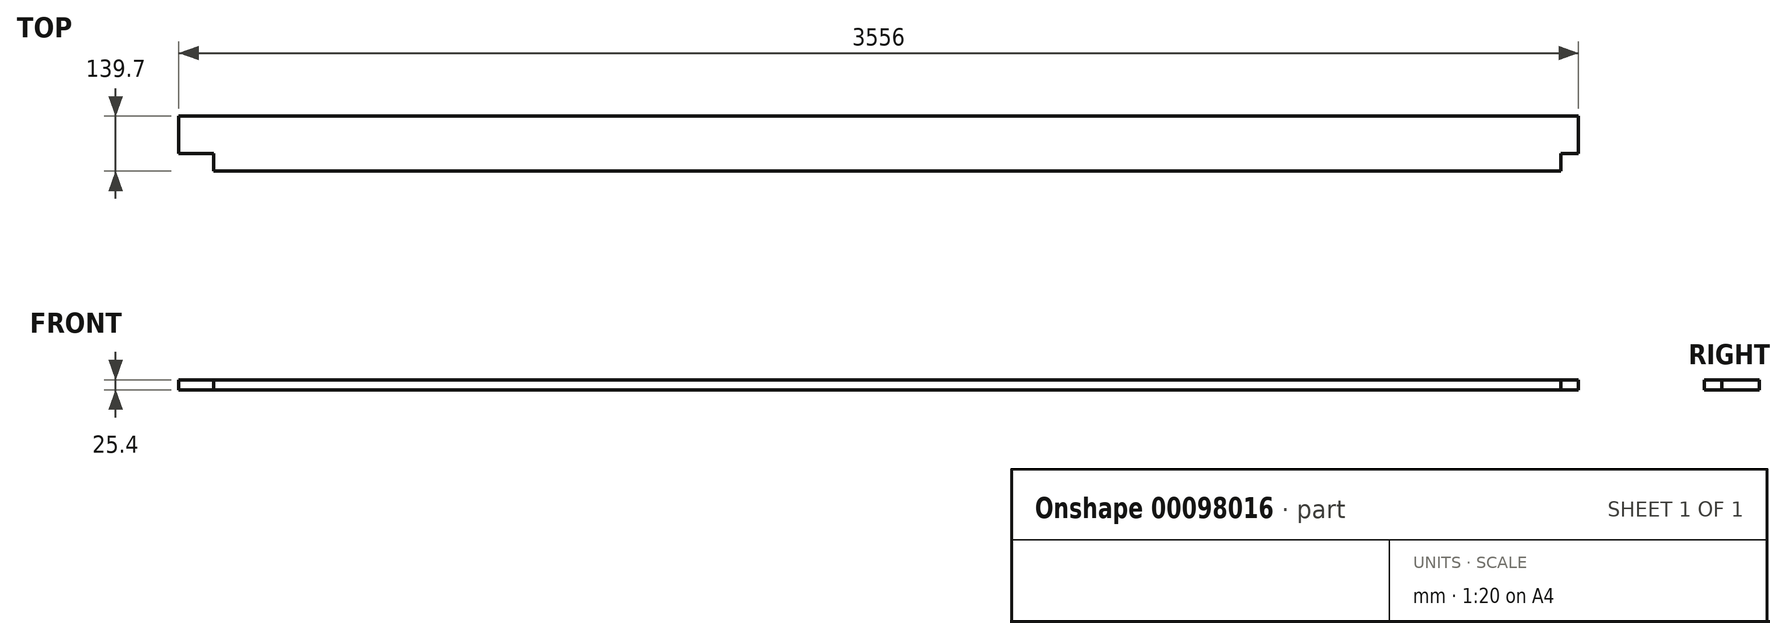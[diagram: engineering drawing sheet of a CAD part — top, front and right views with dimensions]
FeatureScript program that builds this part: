
annotation { "Feature Type Name" : "Feature", "Feature Type Description" : "" }
export const myFeature = defineFeature(function(context is Context, id is Id, definition is map)
    precondition{}
    {
        {
            var Q0;
            Q0=qCreatedBy(makeId("Top.planeOp"),FACE);
            var sketch = newSketch(context, id + "F0", { "sketchPlane" : qUnion([Q0])});
            skLineSegment(sketch, "E0.bottom", {"start": v(1778, 69.85) * mm, "end": v(-1778, 69.85) * mm});
            skLineSegment(sketch, "E0.top", {"start": v(1778, -69.85) * mm, "end": v(-1778, -69.85) * mm});
            skLineSegment(sketch, "E0.left", {"start": v(1778, 69.85) * mm, "end": v(1778, -69.85) * mm});
            skLineSegment(sketch, "E0.right", {"start": v(-1778, 69.85) * mm, "end": v(-1778, -69.85) * mm});
            skPoint(sketch, "E0.middle", {"position": v(0, 0) * mm});
            skSolve(sketch);
        }
        {
            var Q0;
            Q0=makeQuery(id+"F0.imprint","IMPRINT",FACE,{"disambiguationData":[TD([[makeQuery(id+"F0.imprint","IMPRINT",EDGE,{"derivedFrom":sQuery(id+"F0.wireOp",EDGE,"E0.bottom")}),1.0]])]});
            extrude(context, id + "F1", {"entities" : qUnion([Q0]), "depth" : 25.4 * mm});
        }
        {
            var Q0;
            Q0=makeQuery(id+"F1.opExtrude","CAP_FACE",FACE,{"disambiguationData":[OSD([sQuery(id+"F0.wireOp",EDGE,"E0.bottom"),sQuery(id+"F0.wireOp",EDGE,"E0.top"),sQuery(id+"F0.wireOp",EDGE,"E0.left"),sQuery(id+"F0.wireOp",EDGE,"E0.right")])],"isStart":false});
            var sketch = newSketch(context, id + "F2", { "sketchPlane" : qUnion([Q0])});
            skLineSegment(sketch, "E1", {"start": v(-1778, -69.85) * mm, "end": v(-1778, -25.4) * mm});
            skLineSegment(sketch, "E2", {"start": v(-1778, -25.4) * mm, "end": v(-1689.1, -25.4) * mm});
            skLineSegment(sketch, "E3", {"start": v(-1689.1, -25.4) * mm, "end": v(-1689.1, -69.85) * mm});
            skLineSegment(sketch, "E4", {"start": v(-1689.1, -69.85) * mm, "end": v(-1778, -69.85) * mm});
            skSolve(sketch);
        }
        {
            var Q0;
            Q0 = qSketchRegion(id + "F2", true);
            extrude(context, id + "F3", {"entities" : qUnion([Q0]), "operationType" : NewBodyOperationType.REMOVE, "endBound" : BoundingType.THROUGH_ALL, "oppositeDirection" : true, "depth" : 25.4 * mm});
        }
        {
            var Q0;
            Q0=makeQuery(id+"F1.opExtrude","CAP_FACE",FACE,{"disambiguationData":[OSD([sQuery(id+"F0.wireOp",EDGE,"E0.bottom"),sQuery(id+"F0.wireOp",EDGE,"E0.top"),sQuery(id+"F0.wireOp",EDGE,"E0.left"),sQuery(id+"F0.wireOp",EDGE,"E0.right")])],"isStart":false});
            var sketch = newSketch(context, id + "F4", { "sketchPlane" : qUnion([Q0])});
            skLineSegment(sketch, "E5", {"start": v(1778, -69.85) * mm, "end": v(1778, -25.4) * mm});
            skLineSegment(sketch, "E6", {"start": v(1778, -25.4) * mm, "end": v(1733.55, -25.4) * mm});
            skLineSegment(sketch, "E7", {"start": v(1733.55, -25.4) * mm, "end": v(1733.55, -69.85) * mm});
            skLineSegment(sketch, "E8", {"start": v(1733.55, -69.85) * mm, "end": v(1778, -69.85) * mm});
            skSolve(sketch);
        }
        {
            var Q0;
            Q0 = qSketchRegion(id + "F4", true);
            extrude(context, id + "F5", {"entities" : qUnion([Q0]), "operationType" : NewBodyOperationType.REMOVE, "endBound" : BoundingType.THROUGH_ALL, "oppositeDirection" : true, "depth" : 25.4 * mm});
        }
    });
